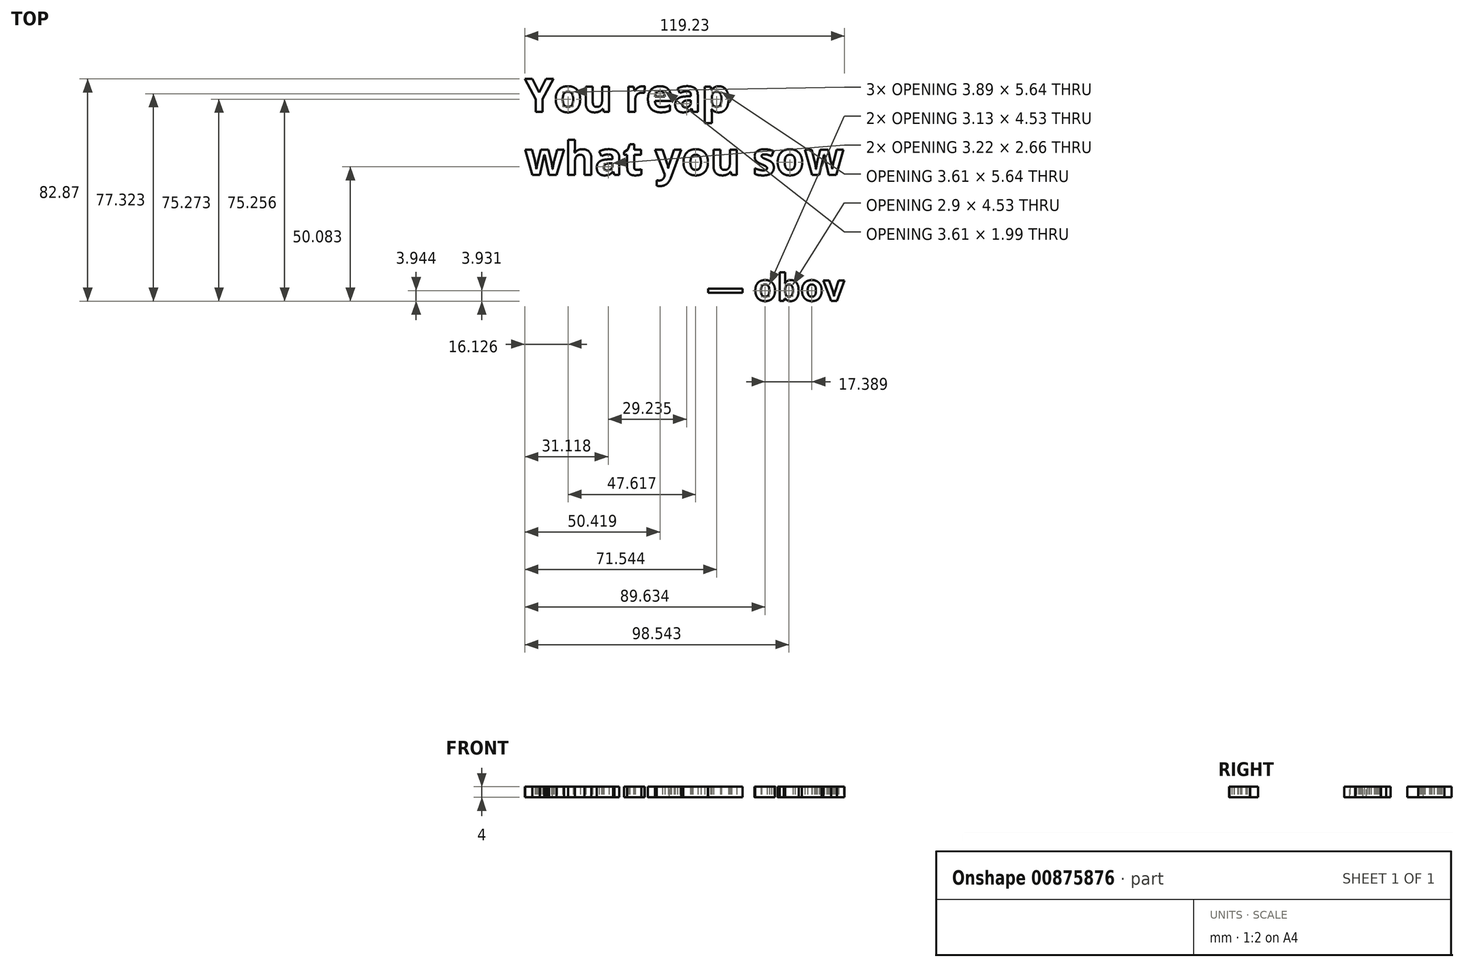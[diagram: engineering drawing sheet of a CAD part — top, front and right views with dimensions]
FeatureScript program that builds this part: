
annotation { "Feature Type Name" : "Feature", "Feature Type Description" : "" }
export const myFeature = defineFeature(function(context is Context, id is Id, definition is map)
    precondition{}
    {
        {
            var Q0;
            Q0=qCreatedBy(makeId("Top.planeOp"),FACE);
            var sketch = newSketch(context, id + "F0", { "sketchPlane" : qUnion([Q0])});
            skText(sketch, "E0", { "text": "You reap \nwhat you sow", "fontName": "OpenSans-Bold.ttf"});
            skText(sketch, "E1", { "text": "— obov", "fontName": "OpenSans-Bold.ttf"});
            const initialGuessF0  = {"E0": [-0.05984, 0.02251, 1, 0, 0.01244], "E1": [0.008, -0.04789, 1, 0, 0.01]};
            skSetInitialGuess(sketch, initialGuessF0);
            skSolve(sketch);
        }
        {
            var Q0;
            Q0 = qSketchRegion(id + "F0", true);
            extrude(context, id + "F1", {"entities" : qUnion([Q0]), "depth" : 4 * mm, "offsetDistance" : 25 * mm});
        }
    });
